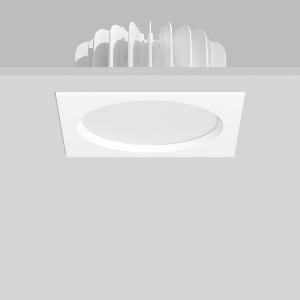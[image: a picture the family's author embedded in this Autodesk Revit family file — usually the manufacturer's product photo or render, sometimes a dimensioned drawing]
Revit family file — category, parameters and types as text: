
# Revit family: ledona_eco_square_901455_002_1_ea8e
name_source: partatom
category: Lighting Fixtures
units: mm (PartAtom-declared; Revit-internal decimal feet)

## family parameters
Cut with Voids When Loaded = No
Host = Face
Light Source = No
Part Type = Normal
Room Calculation Point = No
Round Connector Dimension = Use Diameter
Shared = No

## types (1)
- LEDONA ECO square (1 x LED Modul 840, 2400 lm, 4000)
    Apparent Load = 30 VA
    CIE Flux Codes = 48 81 97 100 100
    Color Rendering = 80
    Color Temperature = 4000
    Default Elevation = 1800 mm
    Height = 0 mm  [stored 0 ft]
    Lamp = 1 x LED Modul 840
    Lamp Light Flux = 2400 lm
    Lamp count = 1
    Length = 220 mm
    Lifetime = 50000 h
    Luminous efficacy = 80 lm/W
    Manufacturer = RZB
    ModVariant = No
    Model = 901455.002.1
    Mounting Place = Ceiling
    Mounting Type = Recessed
    Number of Poles = 1
    OnlyDefault = Yes
    Power Factor = 1
    Product Name = LEDONA ECO square
    Product group = Recessed downlights
    ProductGroupID = 402
    Protection Class = Protection class I
    Protection Degree = IP 65
    RLX_Detail_Level = 1
    RLX_Emergency_Light_Flux = 0 lm
    RLX_Emergency_Type = 0
    RLX_Emergency_Type_DB = No
    RlxData = <blob elided: 35361 chars, md5=adf22223>
    Socket = socket
    Standby Power = 0 W
    System Light Flux = 2400 lm
    System Power = 30 W
    Type Comments = Product without accessories
    Type Image = 901455.002.jpg
    URL = http://relux.com
    VarID = ---
    Voltage = 230 V
    Voltage Range = 220-240 V
    Weight = 0.00 kg
    Width = 220 mm

note: [stored X ft] marks values corroborated as IEEE doubles in the binary element streams (Revit-internal decimal feet)

## geometry (parser evidence)
native form markers: Blend x4, Sweep x10
no freeform markers — native parametric forms only
